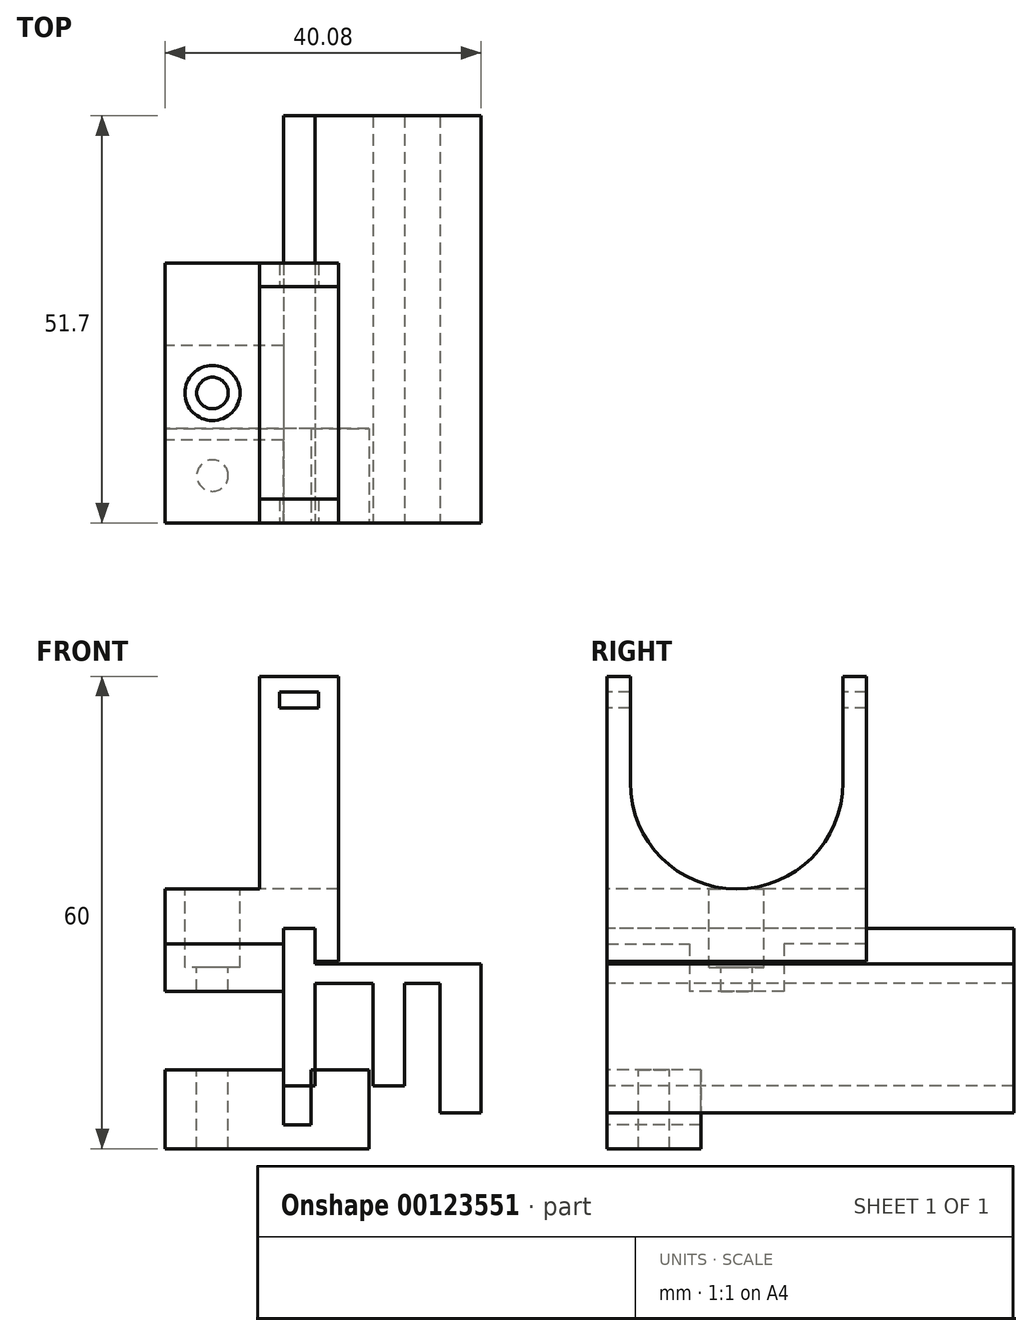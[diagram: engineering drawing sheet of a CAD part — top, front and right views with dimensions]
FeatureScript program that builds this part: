
annotation { "Feature Type Name" : "Feature", "Feature Type Description" : "" }
export const myFeature = defineFeature(function(context is Context, id is Id, definition is map)
    precondition{}
    {
        {
            var Q0;
            Q0=qCreatedBy(makeId("Front.planeOp"),FACE);
            var sketch = newSketch(context, id + "F0", { "sketchPlane" : qUnion([Q0])});
            skLineSegment(sketch, "E0", {"start": v(0, 0) * mm, "end": v(0, -13) * mm});
            skLineSegment(sketch, "E1", {"start": v(0, -13) * mm, "end": v(-4, -13) * mm});
            skLineSegment(sketch, "E2", {"start": v(-4, -13) * mm, "end": v(-4, 7) * mm});
            skLineSegment(sketch, "E3", {"start": v(-4, 7) * mm, "end": v(0, 7) * mm});
            skLineSegment(sketch, "E4", {"start": v(0, 7) * mm, "end": v(0, 2.5) * mm});
            skLineSegment(sketch, "E5", {"start": v(0, 2.5) * mm, "end": v(21.08, 2.5) * mm});
            skLineSegment(sketch, "E6", {"start": v(21.08, 2.5) * mm, "end": v(21.08, -16.43) * mm});
            skLineSegment(sketch, "E7", {"start": v(21.08, -16.43) * mm, "end": v(15.9, -16.43) * mm});
            skLineSegment(sketch, "E8", {"start": v(15.9, -16.43) * mm, "end": v(15.9, 0) * mm});
            skLineSegment(sketch, "E9", {"start": v(15.9, 0) * mm, "end": v(11.4, 0) * mm});
            skLineSegment(sketch, "E10", {"start": v(11.4, 0) * mm, "end": v(11.4, -13) * mm});
            skLineSegment(sketch, "E11", {"start": v(11.4, -13) * mm, "end": v(7.4, -13) * mm});
            skLineSegment(sketch, "E12", {"start": v(7.4, -13) * mm, "end": v(7.4, 0) * mm});
            skLineSegment(sketch, "E13", {"start": v(7.4, 0) * mm, "end": v(0, 0) * mm});
            skSolve(sketch);
        }
        {
            var Q0;
            Q0 = qSketchRegion(id + "F0", true);
            extrude(context, id + "F1", {"entities" : qUnion([Q0]), "oppositeDirection" : true, "depth" : 51.7 * mm});
        }
        {
            var Q0;
            Q0=qCreatedBy(makeId("Front.planeOp"),FACE);
            var sketch = newSketch(context, id + "F2", { "sketchPlane" : qUnion([Q0])});
            skLineSegment(sketch, "E14.0", {"start": v(-0.5, -18) * mm, "end": v(-4, -18) * mm});
            skLineSegment(sketch, "E15.0", {"start": v(-4, 7) * mm, "end": v(0, 7) * mm});
            skLineSegment(sketch, "E16", {"start": v(-0.5, -18) * mm, "end": v(-0.5, -11) * mm});
            skLineSegment(sketch, "E17", {"start": v(-0.5, -11) * mm, "end": v(6.9, -11) * mm});
            skLineSegment(sketch, "E18", {"start": v(6.9, -21) * mm, "end": v(-19, -21) * mm});
            skLineSegment(sketch, "E19", {"start": v(-19, -21) * mm, "end": v(-19, -11) * mm});
            skLineSegment(sketch, "E20", {"start": v(-19, -11) * mm, "end": v(-4, -11) * mm});
            skLineSegment(sketch, "E21", {"start": v(-4, -11) * mm, "end": v(-4, -18) * mm});
            skLineSegment(sketch, "E22", {"start": v(-4, 7) * mm, "end": v(-4, -1) * mm});
            skLineSegment(sketch, "E23", {"start": v(-4, -1) * mm, "end": v(-19, -1) * mm});
            skLineSegment(sketch, "E24", {"start": v(-19, -1) * mm, "end": v(-19, 12) * mm});
            skLineSegment(sketch, "E25", {"start": v(-19, 12) * mm, "end": v(-7, 12) * mm});
            skLineSegment(sketch, "E26", {"start": v(-7, 12) * mm, "end": v(-7, 39) * mm});
            skLineSegment(sketch, "E27", {"start": v(-7, 39) * mm, "end": v(3, 39) * mm});
            skLineSegment(sketch, "E28", {"start": v(3, 39) * mm, "end": v(3, 2.8) * mm});
            skLineSegment(sketch, "E29", {"start": v(3, 2.8) * mm, "end": v(0, 2.8) * mm});
            skLineSegment(sketch, "E30", {"start": v(0, 2.8) * mm, "end": v(0, 7) * mm});
            skLineSegment(sketch, "E31", {"start": v(6.9, -11) * mm, "end": v(6.9, -21) * mm});
            skSolve(sketch);
        }
        {
            var Q0;
            Q0=makeQuery(id+"F2.imprint","IMPRINT",FACE,{"disambiguationData":[TD([[makeQuery(id+"F2.imprint","IMPRINT",EDGE,{"derivedFrom":sQuery(id+"F2.wireOp",EDGE,"E15.0")}),1.0]])]});
            extrude(context, id + "F3", {"entities" : qUnion([Q0]), "oppositeDirection" : true, "depth" : 33 * mm});
        }
        {
            var Q0;
            Q0=makeQuery(id+"F2.imprint","IMPRINT",FACE,{"disambiguationData":[TD([[makeQuery(id+"F2.imprint","IMPRINT",EDGE,{"derivedFrom":sQuery(id+"F2.wireOp",EDGE,"E14.0")}),1.0]])]});
            extrude(context, id + "F4", {"entities" : qUnion([Q0]), "oppositeDirection" : true, "depth" : 12 * mm});
        }
        {
            var Q0;
            Q0=makeQuery(id+"F4.opExtrude","SWEPT_FACE",FACE,{"disambiguationData":[OSD([sQuery(id+"F2.wireOp",EDGE,"E20")])]});
            var sketch = newSketch(context, id + "F5", { "sketchPlane" : qUnion([Q0])});
            skLineSegment(sketch, "E32.0", {"start": v(-19, 12) * mm, "end": v(-19, 0) * mm});
            skLineSegment(sketch, "E33", {"start": v(-19, 6) * mm, "end": v(-13, 6) * mm, "construction": true});
            skCircle(sketch, "E34", {"center": v(-13, 6) * mm, "radius": 2 * mm});
            skSolve(sketch);
        }
        {
            var Q0;
            Q0=makeQuery(id+"F5.imprint","IMPRINT",FACE,{"disambiguationData":[TD([[makeQuery(id+"F5.imprint","IMPRINT",EDGE,{"derivedFrom":sQuery(id+"F5.wireOp",EDGE,"E34")}),1.0]])]});
            extrude(context, id + "F6", {"entities" : qUnion([Q0]), "operationType" : NewBodyOperationType.REMOVE, "endBound" : BoundingType.THROUGH_ALL, "oppositeDirection" : true, "depth" : 25 * mm});
        }
        {
            var Q0;
            Q0=makeQuery(id+"F3.opExtrude","SWEPT_FACE",FACE,{"disambiguationData":[OSD([sQuery(id+"F2.wireOp",EDGE,"E25")])]});
            var sketch = newSketch(context, id + "F7", { "sketchPlane" : qUnion([Q0])});
            skLineSegment(sketch, "E35", {"start": v(-19, 16.5) * mm, "end": v(-13, 16.5) * mm, "construction": true});
            skCircle(sketch, "E36", {"center": v(-13, 16.5) * mm, "radius": 3.5 * mm});
            skCircle(sketch, "E37", {"center": v(-13, 16.5) * mm, "radius": 2 * mm});
            skSolve(sketch);
        }
        {
            var Q0;
            Q0=makeQuery(id+"F7.imprint","IMPRINT",FACE,{"disambiguationData":[TD([[makeQuery(id+"F7.imprint","IMPRINT",EDGE,{"derivedFrom":sQuery(id+"F7.wireOp",EDGE,"E37")}),1.0]])]});
            extrude(context, id + "F8", {"entities" : qUnion([Q0]), "operationType" : NewBodyOperationType.REMOVE, "endBound" : BoundingType.THROUGH_ALL, "oppositeDirection" : true, "depth" : 25 * mm});
        }
        {
            var Q0;
            Q0=makeQuery(id+"F7.imprint","IMPRINT",FACE,{"disambiguationData":[TD([[makeQuery(id+"F7.imprint","IMPRINT",EDGE,{"derivedFrom":sQuery(id+"F7.wireOp",EDGE,"E36")}),1.0]])]});
            extrude(context, id + "F9", {"entities" : qUnion([Q0]), "operationType" : NewBodyOperationType.REMOVE, "oppositeDirection" : true, "depth" : 10 * mm});
        }
        {
            var Q0;
            Q0=makeQuery(id+"F3.opExtrude","SWEPT_FACE",FACE,{"disambiguationData":[OSD([sQuery(id+"F2.wireOp",EDGE,"E26")])]});
            var sketch = newSketch(context, id + "F10", { "sketchPlane" : qUnion([Q0])});
            skLineSegment(sketch, "E38.0", {"start": v(-30, 39) * mm, "end": v(-3, 39) * mm});
            skPoint(sketch, "E39.endSnap0", {"position": v(-16.5, 39) * mm});
            skArc(sketch, "E40", {"start": v(-30, 25.5) * mm, "mid": v(-16.5, 12) * mm, "end": v(-3, 25.5) * mm});
            skLineSegment(sketch, "E41", {"start": v(-3, 25.5) * mm, "end": v(-3, 39) * mm});
            skLineSegment(sketch, "E42", {"start": v(-30, 25.5) * mm, "end": v(-30, 39) * mm});
            skPoint(sketch, "E43.orphan", {"position": v(-33, 39) * mm});
            skPoint(sketch, "E44.orphan", {"position": v(0, 39) * mm});
            skSolve(sketch);
        }
        {
            var Q0;
            Q0=makeQuery(id+"F10.imprint","IMPRINT",FACE,{"disambiguationData":[TD([[makeQuery(id+"F10.imprint","IMPRINT",EDGE,{"derivedFrom":sQuery(id+"F10.wireOp",EDGE,"E38.0")}),-1.0]])]});
            extrude(context, id + "F11", {"entities" : qUnion([Q0]), "operationType" : NewBodyOperationType.REMOVE, "endBound" : BoundingType.THROUGH_ALL, "oppositeDirection" : true, "depth" : 25 * mm});
        }
        {
            var Q0;
            Q0=makeQuery(id+"F3.opExtrude","CAP_FACE",FACE,{"disambiguationData":[OSD([sQuery(id+"F2.wireOp",EDGE,"E15.0"),sQuery(id+"F2.wireOp",EDGE,"E22"),sQuery(id+"F2.wireOp",EDGE,"E23"),sQuery(id+"F2.wireOp",EDGE,"E24"),sQuery(id+"F2.wireOp",EDGE,"E25"),sQuery(id+"F2.wireOp",EDGE,"E26"),sQuery(id+"F2.wireOp",EDGE,"E27"),sQuery(id+"F2.wireOp",EDGE,"E28"),sQuery(id+"F2.wireOp",EDGE,"E29"),sQuery(id+"F2.wireOp",EDGE,"E30")])],"isStart":true});
            var sketch = newSketch(context, id + "F12", { "sketchPlane" : qUnion([Q0])});
            skLineSegment(sketch, "E45.0", {"start": v(-7, 39) * mm, "end": v(3, 39) * mm});
            skLineSegment(sketch, "E46", {"start": v(-2, 39) * mm, "end": v(-2, 36) * mm, "construction": true});
            skLineSegment(sketch, "E47.bottom", {"start": v(0.5, 37) * mm, "end": v(-4.5, 37) * mm});
            skLineSegment(sketch, "E47.top", {"start": v(0.5, 35) * mm, "end": v(-4.5, 35) * mm});
            skLineSegment(sketch, "E47.left", {"start": v(0.5, 37) * mm, "end": v(0.5, 35) * mm});
            skLineSegment(sketch, "E47.right", {"start": v(-4.5, 37) * mm, "end": v(-4.5, 35) * mm});
            skPoint(sketch, "E47.middle", {"position": v(-2, 36) * mm});
            skSolve(sketch);
        }
        {
            var Q0;
            Q0=makeQuery(id+"F12.imprint","IMPRINT",FACE,{"disambiguationData":[TD([[makeQuery(id+"F12.imprint","IMPRINT",EDGE,{"derivedFrom":sQuery(id+"F12.wireOp",EDGE,"E47.bottom")}),1.0]])]});
            extrude(context, id + "F13", {"entities" : qUnion([Q0]), "operationType" : NewBodyOperationType.REMOVE, "endBound" : BoundingType.THROUGH_ALL, "oppositeDirection" : true, "depth" : 25 * mm});
        }
        {
            var Q0;
            Q0=makeQuery(id+"F3.opExtrude","SWEPT_FACE",FACE,{"disambiguationData":[OSD([sQuery(id+"F2.wireOp",EDGE,"E24")])]});
            var sketch = newSketch(context, id + "F14", { "sketchPlane" : qUnion([Q0])});
            skLineSegment(sketch, "E48", {"start": v(-33, -1) * mm, "end": v(-22.5, -1) * mm});
            skLineSegment(sketch, "E49", {"start": v(-22.5, -1) * mm, "end": v(-22.5, 5) * mm});
            skLineSegment(sketch, "E50", {"start": v(-22.5, 5) * mm, "end": v(-33, 5) * mm});
            skLineSegment(sketch, "E51", {"start": v(-16.5, -1) * mm, "end": v(-16.5, 12) * mm, "construction": true});
            skLineSegment(sketch, "E52.MirrorCS", {"start": v(-10.5, -1) * mm, "end": v(-10.5, 5) * mm});
            skLineSegment(sketch, "E53.MirrorCS", {"start": v(0, -1) * mm, "end": v(-10.5, -1) * mm});
            skLineSegment(sketch, "E54.MirrorCS", {"start": v(-10.5, 5) * mm, "end": v(0, 5) * mm});
            skSolve(sketch);
        }
        {
            var Q0;
            {var subQ0=sQuery(id+"F14.wireOp",EDGE,"E48");Q0=makeQuery(id+"F14.imprint","IMPRINT",FACE,{"disambiguationData":[TD([[makeQuery(id+"F14.imprint","IMPRINT",EDGE,{"derivedFrom":subQ0}),1.0]])]});}
            var Q1;
            Q1=makeQuery(id+"F14.imprint","IMPRINT",FACE,{"disambiguationData":[TD([[makeQuery(id+"F14.imprint","IMPRINT",EDGE,{"derivedFrom":sQuery(id+"F14.wireOp",EDGE,"E52.MirrorCS")}),-1.0]])]});
            extrude(context, id + "F15", {"entities" : qUnion([Q0, Q1]), "operationType" : NewBodyOperationType.REMOVE, "endBound" : BoundingType.UP_TO_NEXT, "oppositeDirection" : true, "depth" : 25 * mm});
        }
    });
